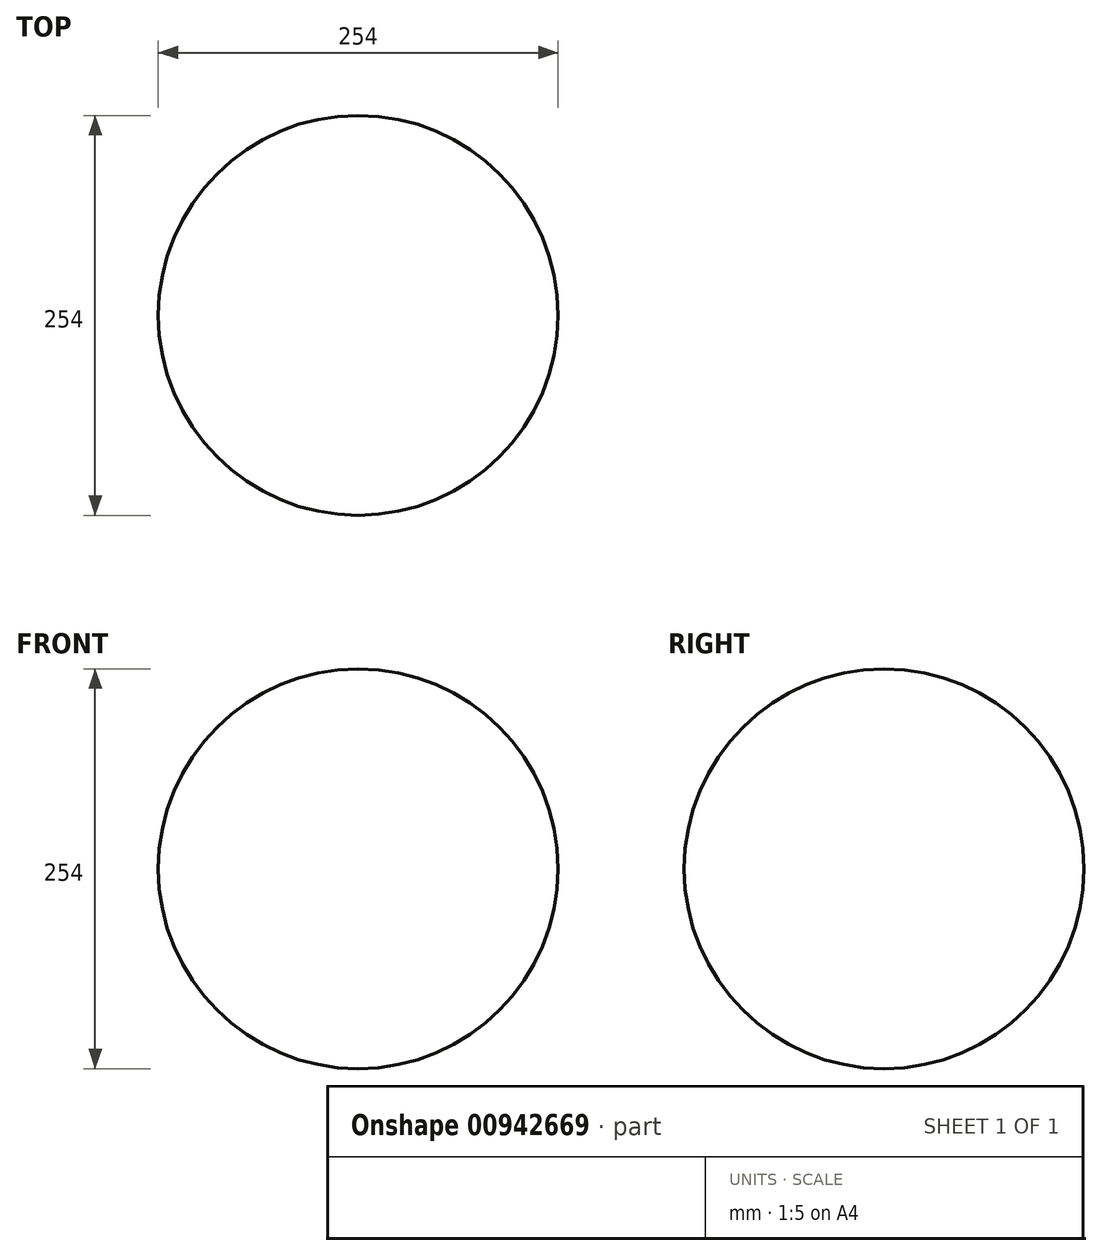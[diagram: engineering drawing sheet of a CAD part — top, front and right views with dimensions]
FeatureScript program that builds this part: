
annotation { "Feature Type Name" : "Feature", "Feature Type Description" : "" }
export const myFeature = defineFeature(function(context is Context, id is Id, definition is map)
    precondition{}
    {
        {
            var Q0;
            Q0=qCreatedBy(makeId("Front.planeOp"),FACE);
            var sketch = newSketch(context, id + "F0", { "sketchPlane" : qUnion([Q0])});
            skLineSegment(sketch, "E0", {"start": v(0, 127) * mm, "end": v(0, -127) * mm});
            skArc(sketch, "E1", {"start": v(0, -127) * mm, "mid": v(127, 0) * mm, "end": v(0, 127) * mm});
            skSolve(sketch);
        }
        {
            var Q0;
            Q0=makeQuery(id+"F0.imprint","IMPRINT",FACE,{"disambiguationData":[TD([[makeQuery(id+"F0.imprint","IMPRINT",EDGE,{"derivedFrom":sQuery(id+"F0.wireOp",EDGE,"E0")}),1.0]])]});
            var Q1;
            Q1=sQuery(id+"F0.wireOp",EDGE,"E0");
            revolve(context, id + "F1", {"surfaceOperationType" : NewSurfaceOperationType.NEW, "entities" : qUnion([Q0]), "axis" : qUnion([Q1]), "revolveType" : RevolveType.FULL});
        }
    });
